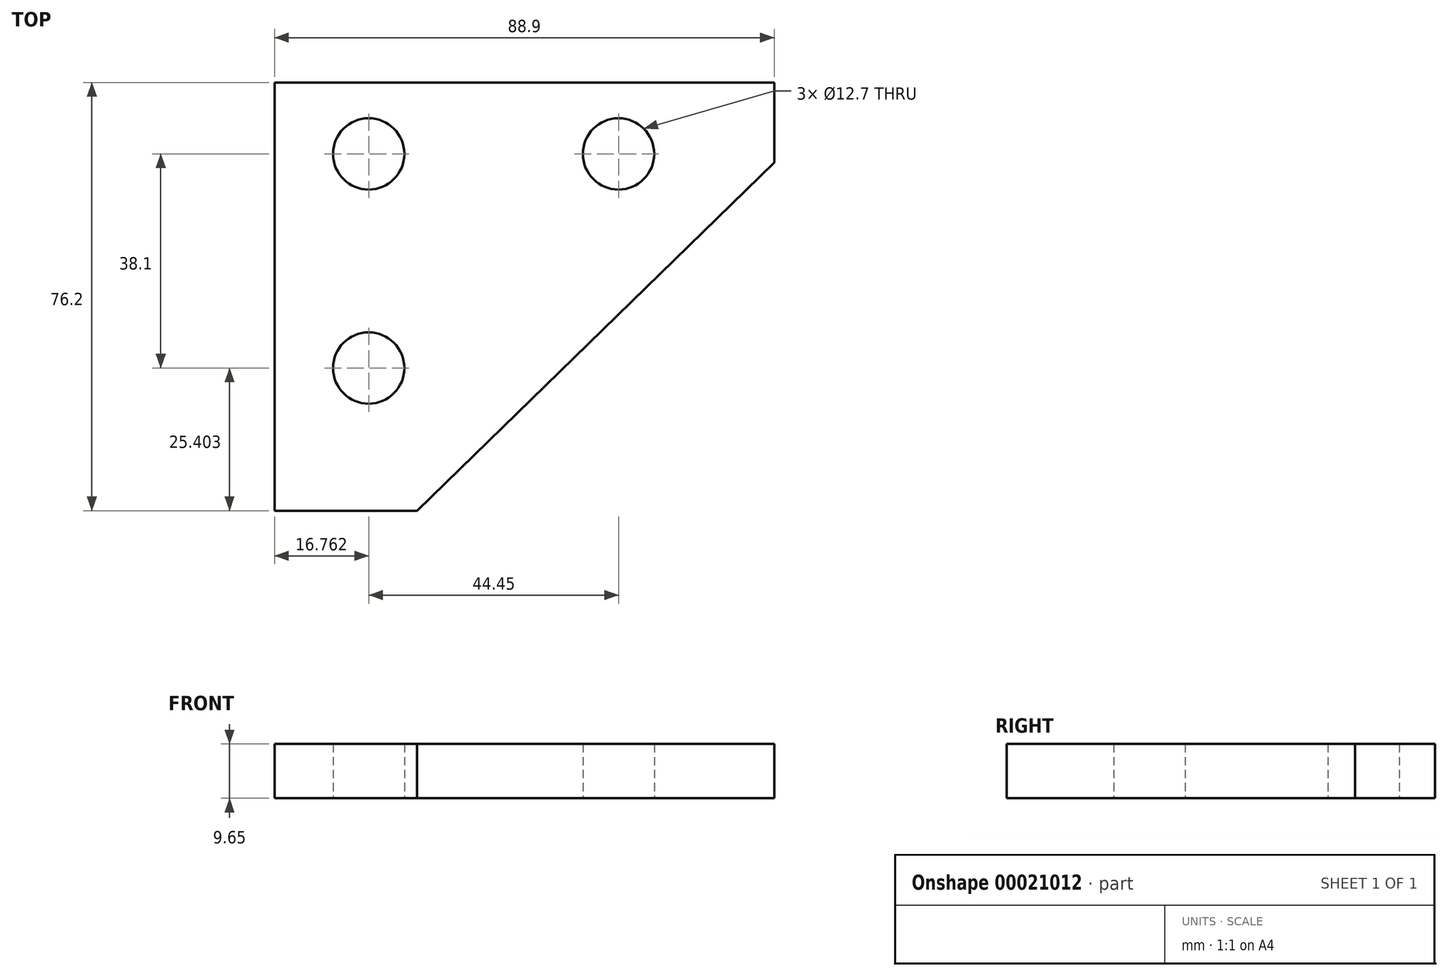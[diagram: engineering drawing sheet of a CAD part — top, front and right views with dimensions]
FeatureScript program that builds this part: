
annotation { "Feature Type Name" : "Feature", "Feature Type Description" : "" }
export const myFeature = defineFeature(function(context is Context, id is Id, definition is map)
    precondition{}
    {
        {
            var Q0;
            Q0=qCreatedBy(makeId("Top.planeOp"),FACE);
            var sketch = newSketch(context, id + "F0", { "sketchPlane" : qUnion([Q0])});
            skLineSegment(sketch, "E0", {"start": v(-46.46, 46.45) * mm, "end": v(42.44, 46.45) * mm});
            skLineSegment(sketch, "E1", {"start": v(42.44, 46.45) * mm, "end": v(42.44, 32.23) * mm});
            skLineSegment(sketch, "E2", {"start": v(42.44, 32.23) * mm, "end": v(-21.06, -29.75) * mm});
            skLineSegment(sketch, "E3", {"start": v(-21.06, -29.75) * mm, "end": v(-46.46, -29.75) * mm});
            skLineSegment(sketch, "E4", {"start": v(-46.46, -29.75) * mm, "end": v(-46.46, 46.45) * mm});
            skCircle(sketch, "E5", {"center": v(-29.7, -4.35) * mm, "radius": 6.35 * mm});
            skCircle(sketch, "E6", {"center": v(-29.7, 33.75) * mm, "radius": 6.35 * mm});
            skCircle(sketch, "E7", {"center": v(14.75, 33.75) * mm, "radius": 6.35 * mm});
            skSolve(sketch);
        }
        {
            var Q0;
            Q0 = qSketchRegion(id + "F0", true);
            extrude(context, id + "F1", {"entities" : qUnion([Q0]), "depth" : 9.65 * mm});
        }
    });
